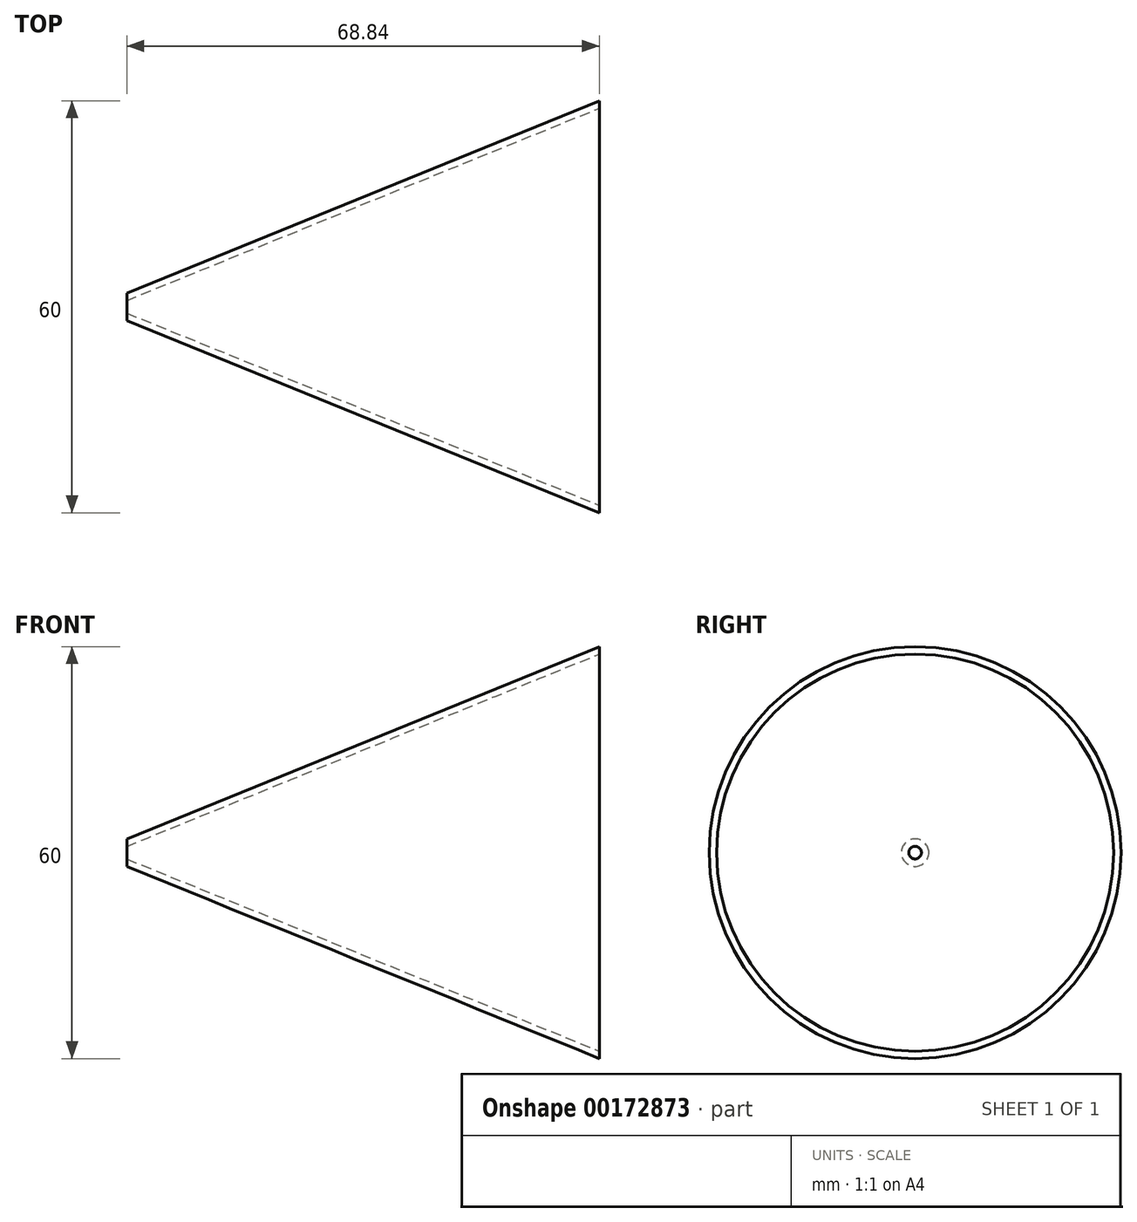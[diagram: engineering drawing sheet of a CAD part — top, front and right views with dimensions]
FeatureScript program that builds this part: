
annotation { "Feature Type Name" : "Feature", "Feature Type Description" : "" }
export const myFeature = defineFeature(function(context is Context, id is Id, definition is map)
    precondition{}
    {
        {
            var Q0;
            Q0=qCreatedBy(makeId("Top.planeOp"),FACE);
            var sketch = newSketch(context, id + "F0", { "sketchPlane" : qUnion([Q0])});
            skLineSegment(sketch, "E0", {"start": v(0, -30) * mm, "end": v(0, 30) * mm});
            skLineSegment(sketch, "E1", {"start": v(0, -30) * mm, "end": v(-68.84, -2) * mm});
            skLineSegment(sketch, "E2", {"start": v(0, 30) * mm, "end": v(-68.84, 2) * mm});
            skLineSegment(sketch, "E3", {"start": v(-68.84, -2) * mm, "end": v(-68.84, 2) * mm});
            skLineSegment(sketch, "E4", {"start": v(0, 0) * mm, "end": v(-68.84, 0) * mm});
            skSolve(sketch);
        }
        {
            var Q0;
            {var subQ0=sQuery(id+"F0.wireOp",EDGE,"E1");Q0=makeQuery(id+"F0.imprint","IMPRINT",FACE,{"disambiguationData":[TD([[makeQuery(id+"F0.imprint","IMPRINT",EDGE,{"derivedFrom":subQ0}),-1.0]])]});}
            var Q1;
            Q1=sQuery(id+"F0.wireOp",EDGE,"E4");
            revolve(context, id + "F1", {"entities" : qUnion([Q0]), "axis" : qUnion([Q1]), "revolveType" : RevolveType.ONE_DIRECTION, "angle" : 360 * degree});
        }
        {
            var Q0;
            Q0=makeQuery(id+"F1.opRevolve","SWEPT_FACE",FACE,{"disambiguationData":[OSD([sQuery(id+"F0.wireOp",EDGE,"E3")])]});
            var Q1;
            Q1=makeQuery(id+"F1.opRevolve","SWEPT_FACE",FACE,{"disambiguationData":[OSD([sQuery(id+"F0.wireOp",EDGE,"E0")])]});
            shell(context, id + "F2", {"entities" : qUnion([Q0, Q1]), "thickness" : 1 * mm});
        }
    });
